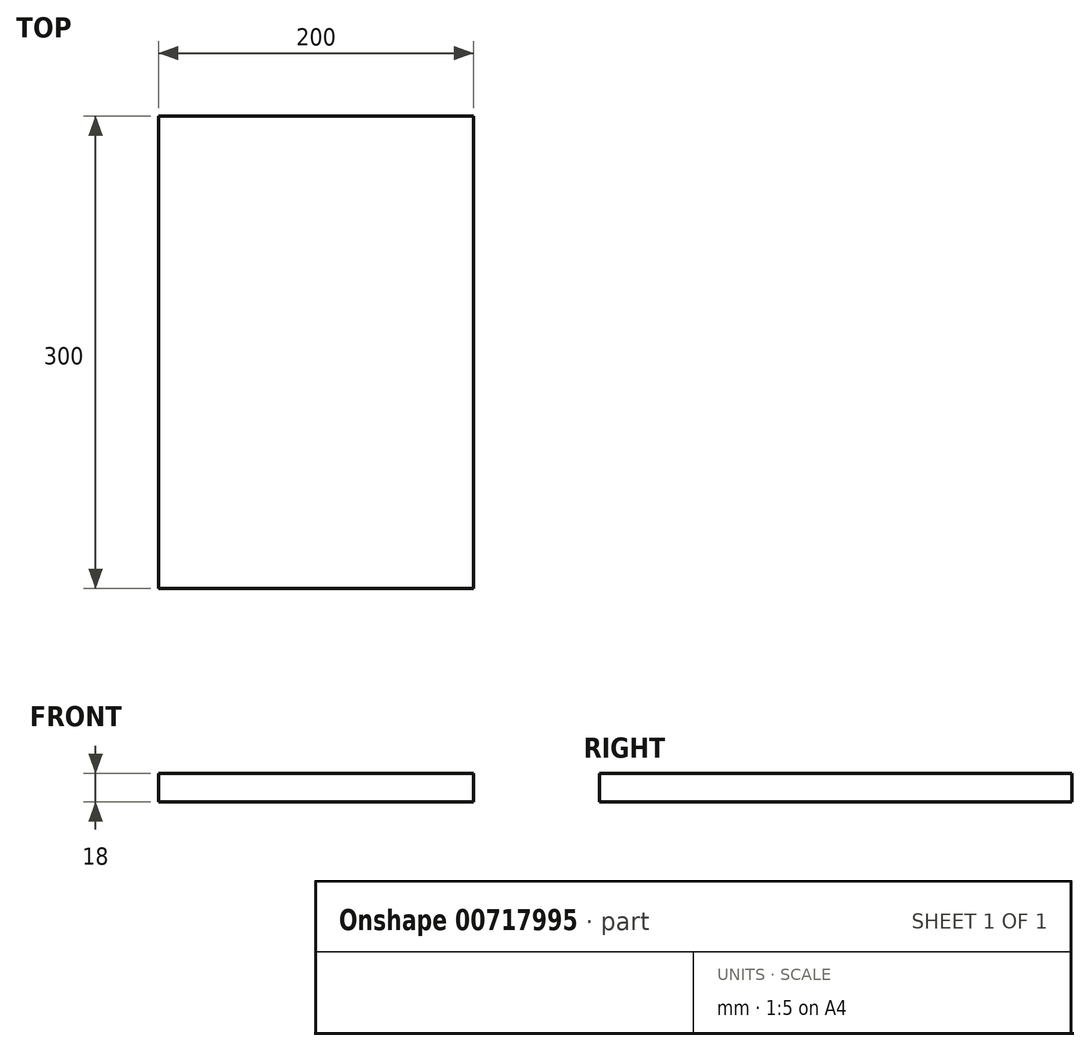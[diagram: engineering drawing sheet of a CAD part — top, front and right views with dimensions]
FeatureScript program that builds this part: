
annotation { "Feature Type Name" : "Feature", "Feature Type Description" : "" }
export const myFeature = defineFeature(function(context is Context, id is Id, definition is map)
    precondition{}
    {
        {
            var Q0;
            Q0=qCreatedBy(makeId("Front.planeOp"),FACE);
            var sketch = newSketch(context, id + "F0", { "sketchPlane" : qUnion([Q0])});
            skLineSegment(sketch, "E0.bottom", {"start": v(0, 0) * mm, "end": v(200, 0) * mm});
            skLineSegment(sketch, "E0.top", {"start": v(0, -18) * mm, "end": v(200, -18) * mm});
            skLineSegment(sketch, "E0.left", {"start": v(0, 0) * mm, "end": v(0, -18) * mm});
            skLineSegment(sketch, "E0.right", {"start": v(200, 0) * mm, "end": v(200, -18) * mm});
            skSolve(sketch);
        }
        {
            var Q0;
            Q0=makeQuery(id+"F0.imprint","IMPRINT",FACE,{"disambiguationData":[TD([[makeQuery(id+"F0.imprint","IMPRINT",EDGE,{"derivedFrom":sQuery(id+"F0.wireOp",EDGE,"E0.bottom")}),-1.0]])]});
            extrude(context, id + "F1", {"entities" : qUnion([Q0]), "depth" : 300 * mm, "offsetDistance" : 25 * mm});
        }
    });
